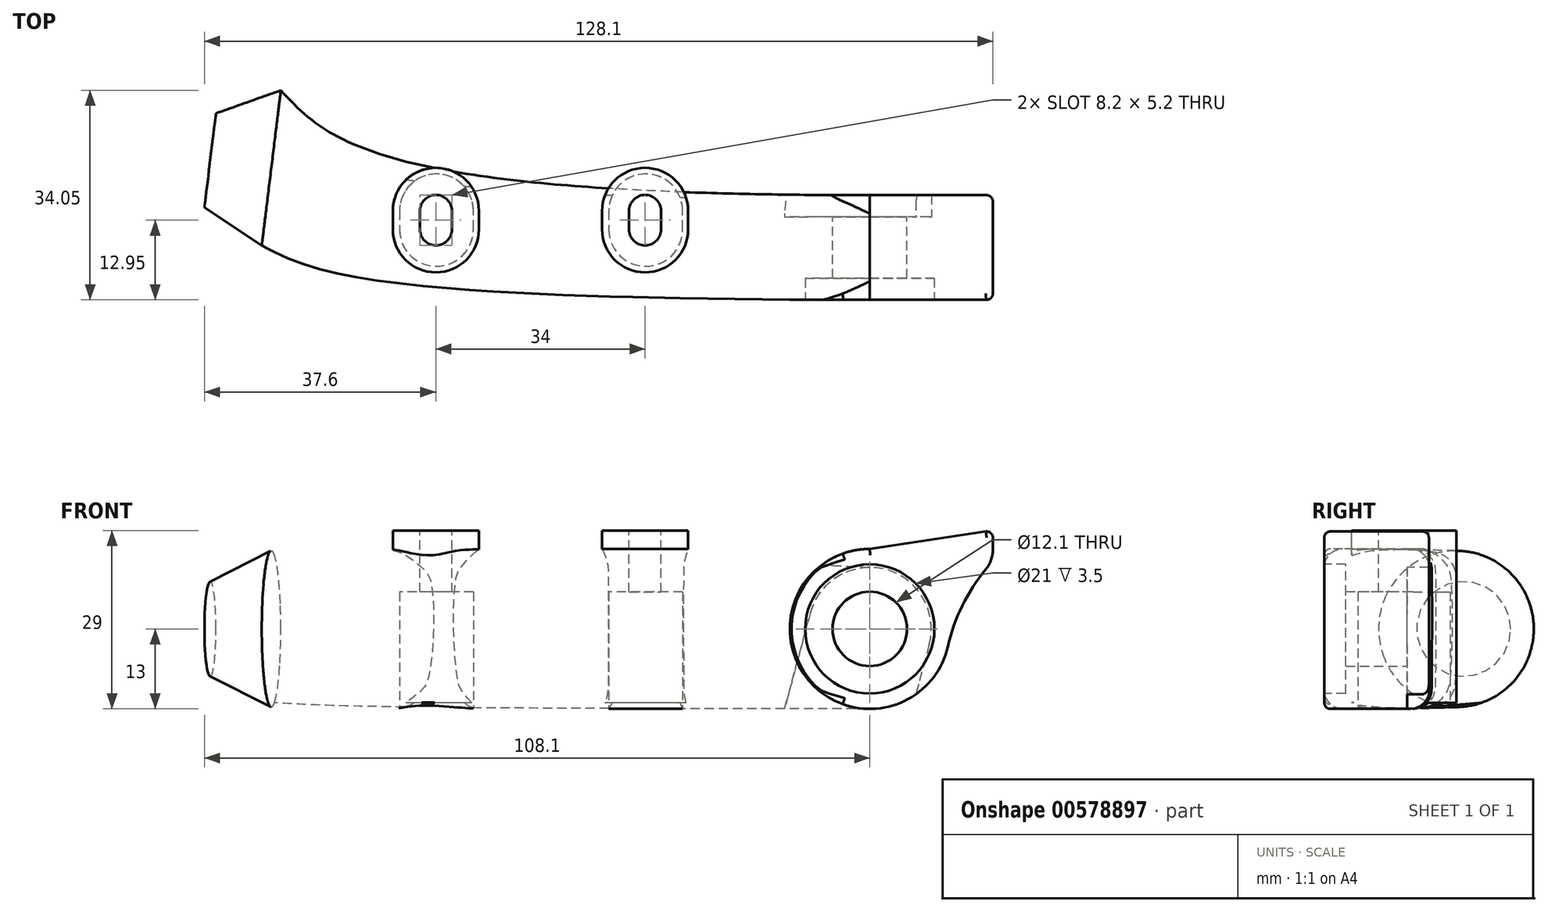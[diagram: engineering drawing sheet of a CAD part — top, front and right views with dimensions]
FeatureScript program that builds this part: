
annotation { "Feature Type Name" : "Feature", "Feature Type Description" : "" }
export const myFeature = defineFeature(function(context is Context, id is Id, definition is map)
    precondition{}
    {
        {
            var Q0;
            Q0=qCreatedBy(makeId("Top.planeOp"),FACE);
            cPlane(context, id + "F0", {"entities" : qUnion([Q0]), "cplaneType" : CPlaneType.OFFSET, "offset" : 16 * mm, "width" : 152.4 * mm, "height" : 152.4 * mm});
        }
        {
            var Q0;
            Q0=qCreatedBy(id+"F0.planeOp",FACE);
            var sketch = newSketch(context, id + "F1", { "sketchPlane" : qUnion([Q0])});
            skArc(sketch, "E0", {"start": v(-39.1, -2.05) * mm, "mid": v(-36.5, -4.65) * mm, "end": v(-33.9, -2.05) * mm});
            skArc(sketch, "E1", {"start": v(-33.9, 0.95) * mm, "mid": v(-36.5, 3.55) * mm, "end": v(-39.1, 0.95) * mm});
            skLineSegment(sketch, "E2", {"start": v(-39.1, -2.05) * mm, "end": v(-39.1, 0.95) * mm});
            skLineSegment(sketch, "E3", {"start": v(-33.9, 0.95) * mm, "end": v(-33.9, -2.05) * mm});
            skArc(sketch, "E4.0", {"start": v(-29.5, 0.95) * mm, "mid": v(-36.5, 7.95) * mm, "end": v(-43.5, 0.95) * mm});
            skLineSegment(sketch, "E4.1", {"start": v(-29.5, 0.95) * mm, "end": v(-29.5, -2.05) * mm});
            skArc(sketch, "E4.2", {"start": v(-43.5, -2.05) * mm, "mid": v(-36.5, -9.05) * mm, "end": v(-29.5, -2.05) * mm});
            skLineSegment(sketch, "E4.3", {"start": v(-43.5, -2.05) * mm, "end": v(-43.5, 0.95) * mm});
            skArc(sketch, "E5", {"start": v(-73.1, -2.05) * mm, "mid": v(-70.5, -4.65) * mm, "end": v(-67.9, -2.05) * mm});
            skArc(sketch, "E6", {"start": v(-67.9, 0.95) * mm, "mid": v(-70.5, 3.55) * mm, "end": v(-73.1, 0.95) * mm});
            skLineSegment(sketch, "E7", {"start": v(-73.1, -2.05) * mm, "end": v(-73.1, 0.95) * mm});
            skLineSegment(sketch, "E8", {"start": v(-67.9, 0.95) * mm, "end": v(-67.9, -2.05) * mm});
            skArc(sketch, "E9.0", {"start": v(-63.5, 0.95) * mm, "mid": v(-70.5, 7.95) * mm, "end": v(-77.5, 0.95) * mm});
            skLineSegment(sketch, "E9.1", {"start": v(-63.5, 0.95) * mm, "end": v(-63.5, -2.05) * mm});
            skArc(sketch, "E9.2", {"start": v(-77.5, -2.05) * mm, "mid": v(-70.5, -9.05) * mm, "end": v(-63.5, -2.05) * mm});
            skLineSegment(sketch, "E9.3", {"start": v(-77.5, -2.05) * mm, "end": v(-77.5, 0.95) * mm});
            skSolve(sketch);
        }
        {
            var Q0;
            Q0=makeQuery(id+"F1.imprint","IMPRINT",FACE,{"disambiguationData":[TD([[makeQuery(id+"F1.imprint","IMPRINT",EDGE,{"derivedFrom":sQuery(id+"F1.wireOp",EDGE,"E5")}),-1.0]])]});
            var Q1;
            Q1=makeQuery(id+"F1.imprint","IMPRINT",FACE,{"disambiguationData":[TD([[makeQuery(id+"F1.imprint","IMPRINT",EDGE,{"derivedFrom":sQuery(id+"F1.wireOp",EDGE,"E0")}),-1.0]])]});
            var Q2;
            {var subQ1=sQuery(id+"F9.wireOp",EDGE,"E18.bottom");var subQ2=sQuery(id+"F9.wireOp",EDGE,"E20.filletArc");var subQ3=sQuery(id+"F9.wireOp",EDGE,"E21.filletArc");var subQ4=sQuery(id+"F8.wireOp",EDGE,"E17");Q2=makeQuery(id+"F11.boolean.opBoolean","SPLIT",FACE,{"disambiguationData":[TD([makeQuery(id+"F11.opLoft","CAP_FACE",FACE,{"disambiguationData":[OSD([makeQuery(id+"F8.imprint","IMPRINT",FACE,{"disambiguationData":[TD([[makeQuery(id+"F8.imprint","IMPRINT",EDGE,{"derivedFrom":subQ4}),1.0]])]})])],"isStart":true})])],"derivedFrom":makeQuery(id+"F11.opLoft","SWEPT_FACE",FACE,{"disambiguationData":[OSD([subQ4,subQ1,subQ2,subQ3])]})});}
            var Q3;
            Q3=makeQuery(id+"F4.opExtrude","SWEPT_BODY",BODY,{"disambiguationData":[OSD([sQuery(id+"F3.wireOp",EDGE,"2tPzwoB9-yS2f-pc6b-ztwz-8XCjIK9uUhir"),sQuery(id+"F3.wireOp",EDGE,"E11"),sQuery(id+"F3.wireOp",EDGE,"te52xsig-TtHM-ymU2-F68U-3UsOK3ld5ssy"),sQuery(id+"F3.wireOp",EDGE,"6Uz9XqtG-uSJd-Klk5-Kt3H-MewUyz8nc5kr")])]});
            extrude(context, id + "F2", {"entities" : qUnion([Q0, Q1]), "oppositeDirection" : true, "depth" : 28 * mm, "endBoundEntityFace" : qUnion([Q2]), "endBoundEntityBody" : qUnion([Q3]), "offsetDistance" : 25 * mm});
        }
        {
            var Q0;
            Q0=qCreatedBy(makeId("Front.planeOp"),FACE);
            var sketch = newSketch(context, id + "F3", { "sketchPlane" : qUnion([Q0])});
            skCircle(sketch, "E10", {"center": v(0, 0) * mm, "radius": 6.05 * mm});
            skCircle(sketch, "E11", {"center": v(0, 0) * mm, "radius": 13 * mm});
            skArc(sketch, "E12", {"start": v(9.66, -2.59) * mm, "mid": v(2.59, 9.66) * mm, "end": v(-9.66, 2.59) * mm});
            skLineSegment(sketch, "E13", {"start": v(9.66, -2.59) * mm, "end": v(3.8, -24.44) * mm});
            skLineSegment(sketch, "E14", {"start": v(3.8, -24.44) * mm, "end": v(-15.51, -19.26) * mm});
            skLineSegment(sketch, "E15", {"start": v(-15.51, -19.26) * mm, "end": v(-9.66, 2.59) * mm});
            skSolve(sketch);
        }
        {
            var Q0;
            Q0=makeQuery(id+"F3.imprint","IMPRINT",FACE,{"disambiguationData":[TD([[makeQuery(id+"F3.imprint","IMPRINT",EDGE,{"derivedFrom":sQuery(id+"F3.wireOp",EDGE,"2tPzwoB9-yS2f-pc6b-ztwz-8XCjIK9uUhir")}),-1.0]])]});
            var Q1;
            {var subQ5=sQuery(id+"F3.wireOp",EDGE,"E12");Q1=makeQuery(id+"F3.imprint","IMPRINT",FACE,{"disambiguationData":[TD([[makeQuery(id+"F3.imprint","IMPRINT",EDGE,{"derivedFrom":subQ5}),-1.0]])]});}
            extrude(context, id + "F4", {"entities" : qUnion([Q0, Q1]), "oppositeDirection" : true, "depth" : 3.5 * mm, "offsetDistance" : 25 * mm});
        }
        {
            var Q0;
            Q0=makeQuery(id+"F3.imprint","IMPRINT",FACE,{"disambiguationData":[TD([[makeQuery(id+"F3.imprint","IMPRINT",EDGE,{"derivedFrom":sQuery(id+"F3.wireOp",EDGE,"E10")}),-1.0]])]});
            var Q1;
            {var subQ5=sQuery(id+"F3.wireOp",EDGE,"E12");Q1=makeQuery(id+"F3.imprint","IMPRINT",FACE,{"disambiguationData":[TD([[makeQuery(id+"F3.imprint","IMPRINT",EDGE,{"derivedFrom":subQ5}),-1.0]])]});}
            extrude(context, id + "F5", {"entities" : qUnion([Q0, Q1]), "operationType" : NewBodyOperationType.ADD, "depth" : 13.5 * mm, "offsetDistance" : 25 * mm});
        }
        {
            var Q0;
            Q0=qCreatedBy(makeId("Top.planeOp"),FACE);
            var sketch = newSketch(context, id + "F6", { "sketchPlane" : qUnion([Q0])});
            skLineSegment(sketch, "E16", {"start": v(-100, -14.56) * mm, "end": v(-96.9, 10.65) * mm});
            skSolve(sketch);
        }
        {
            var Q0;
            Q0=sQuery(id+"F6.wireOp",EDGE,"E16");
            cPlane(context, id + "F7", {"entities" : qUnion([Q0]), "cplaneType" : CPlaneType.LINE_ANGLE, "offset" : 25 * mm, "angle" : 90 * degree, "width" : 150 * mm, "height" : 150 * mm});
        }
        {
            var Q0;
            Q0=qCreatedBy(id+"F7.planeOp",FACE);
            var sketch = newSketch(context, id + "F8", { "sketchPlane" : qUnion([Q0])});
            skCircle(sketch, "E17", {"center": v(-3.97, 0) * mm, "radius": 12.7 * mm});
            skSolve(sketch);
        }
        {
            var Q0;
            Q0=qCreatedBy(makeId("Right.planeOp"),FACE);
            var sketch = newSketch(context, id + "F9", { "sketchPlane" : qUnion([Q0])});
            skLineSegment(sketch, "E18.bottom", {"start": v(0.5, -13) * mm, "end": v(-10.5, -13) * mm});
            skLineSegment(sketch, "E18.top", {"start": v(0.5, 13) * mm, "end": v(-10.5, 13) * mm});
            skLineSegment(sketch, "E18.left", {"start": v(3.5, -10) * mm, "end": v(3.5, 10) * mm});
            skLineSegment(sketch, "E18.right", {"start": v(-13.5, -10) * mm, "end": v(-13.5, 10) * mm});
            skPoint(sketch, "E19.visualSharp", {"position": v(-13.5, 13) * mm});
            skArc(sketch, "E19.filletArc", {"start": v(-10.5, 13) * mm, "mid": v(-12.62, 12.12) * mm, "end": v(-13.5, 10) * mm});
            skPoint(sketch, "E20.visualSharp", {"position": v(-13.5, -13) * mm});
            skArc(sketch, "E20.filletArc", {"start": v(-13.5, -10) * mm, "mid": v(-12.62, -12.12) * mm, "end": v(-10.5, -13) * mm});
            skPoint(sketch, "E21.visualSharp", {"position": v(3.5, -13) * mm});
            skArc(sketch, "E21.filletArc", {"start": v(0.5, -13) * mm, "mid": v(2.62, -12.12) * mm, "end": v(3.5, -10) * mm});
            skPoint(sketch, "E22.visualSharp", {"position": v(3.5, 13) * mm});
            skArc(sketch, "E22.filletArc", {"start": v(3.5, 10) * mm, "mid": v(2.62, 12.12) * mm, "end": v(0.5, 13) * mm});
            skSolve(sketch);
        }
        {
            var Q0;
            Q0=qCreatedBy(makeId("Right.planeOp"),FACE);
            cPlane(context, id + "F10", {"entities" : qUnion([Q0]), "cplaneType" : CPlaneType.OFFSET, "offset" : 20 * mm, "width" : 150 * mm, "height" : 150 * mm});
        }
        {
            var Q0;
            Q0 = qSketchRegion(id + "F9", true);
            var Q1;
            Q1 = qSketchRegion(id + "F8", true);
            loft(context, id + "F11", {"operationType" : NewBodyOperationType.ADD, "startCondition" : LoftEndDerivativeType.NORMAL_TO_PROFILE, "startMagnitude" : 2.5, "sheetProfilesArray" : [{ "sheetProfileEntities" : qUnion([Q0]) }, { "sheetProfileEntities" : qUnion([Q1]) }]});
        }
        {
            var Q0;
            Q0=qCreatedBy(makeId("Right.planeOp"),FACE);
            var sketch = newSketch(context, id + "F12", { "sketchPlane" : qUnion([Q0])});
            skLineSegment(sketch, "E23.bottom", {"start": v(3.5, 0) * mm, "end": v(-13.5, 0) * mm});
            skLineSegment(sketch, "E23.top", {"start": v(3.5, 13) * mm, "end": v(-13.5, 13) * mm});
            skLineSegment(sketch, "E23.left", {"start": v(3.5, 0) * mm, "end": v(3.5, 13) * mm});
            skLineSegment(sketch, "E23.right", {"start": v(-13.5, 0) * mm, "end": v(-13.5, 13) * mm});
            skPoint(sketch, "E24.visualSharp", {"position": v(-13.5, 13) * mm});
            skLineSegment(sketch, "E24.filletArc", {"start": v(-13.5, 13) * mm, "end": v(-13.5, 13) * mm});
            skPoint(sketch, "E25.visualSharp", {"position": v(3.5, 13) * mm});
            skLineSegment(sketch, "E25.filletArc", {"start": v(3.5, 13) * mm, "end": v(3.5, 13) * mm});
            skSolve(sketch);
        }
        {
            var Q0;
            Q0=qCreatedBy(id+"F10.planeOp",FACE);
            var sketch = newSketch(context, id + "F13", { "sketchPlane" : qUnion([Q0])});
            skLineSegment(sketch, "E26.bottom", {"start": v(3.5, 16) * mm, "end": v(-13.5, 16) * mm});
            skLineSegment(sketch, "E26.top", {"start": v(3.5, 11) * mm, "end": v(-13.5, 11) * mm});
            skLineSegment(sketch, "E26.left", {"start": v(3.5, 16) * mm, "end": v(3.5, 11) * mm});
            skLineSegment(sketch, "E26.right", {"start": v(-13.5, 16) * mm, "end": v(-13.5, 11) * mm});
            skSolve(sketch);
        }
        {
            var Q1;
            Q1 = qSketchRegion(id + "F12", true);
            var Q2;
            Q2 = qSketchRegion(id + "F13", true);
            loft(context, id + "F14", {"operationType" : NewBodyOperationType.ADD, "sheetProfilesArray" : [{ "sheetProfileEntities" : qUnion([Q1]) }, { "sheetProfileEntities" : qUnion([Q2]) }]});
        }
        {
            var Q0;
            Q0=makeQuery(id+"F3.imprint","IMPRINT",FACE,{"disambiguationData":[TD([[makeQuery(id+"F3.imprint","IMPRINT",EDGE,{"derivedFrom":sQuery(id+"F3.wireOp",EDGE,"E10")}),-1.0]])]});
            var Q1;
            {var subQ5=sQuery(id+"F3.wireOp",EDGE,"E14");Q1=makeQuery(id+"F3.imprint","IMPRINT",FACE,{"disambiguationData":[TD([[makeQuery(id+"F3.imprint","IMPRINT",EDGE,{"derivedFrom":subQ5}),-1.0]])]});}
            var Q2;
            Q2=makeQuery(id+"F3.imprint","IMPRINT",FACE,{"disambiguationData":[TD([[makeQuery(id+"F3.imprint","IMPRINT",EDGE,{"derivedFrom":sQuery(id+"F3.wireOp",EDGE,"E10")}),1.0]])]});
            extrude(context, id + "F15", {"entities" : qUnion([Q0, Q1, Q2]), "operationType" : NewBodyOperationType.REMOVE, "oppositeDirection" : true, "depth" : 25 * mm, "offsetDistance" : 25 * mm});
        }
        {
            var Q0;
            Q0=makeQuery(id+"F1.imprint","IMPRINT",FACE,{"disambiguationData":[TD([[makeQuery(id+"F1.imprint","IMPRINT",EDGE,{"derivedFrom":sQuery(id+"F1.wireOp",EDGE,"E5")}),1.0]])]});
            var Q1;
            Q1=makeQuery(id+"F1.imprint","IMPRINT",FACE,{"disambiguationData":[TD([[makeQuery(id+"F1.imprint","IMPRINT",EDGE,{"derivedFrom":sQuery(id+"F1.wireOp",EDGE,"E0")}),1.0]])]});
            extrude(context, id + "F16", {"entities" : qUnion([Q0, Q1]), "operationType" : NewBodyOperationType.REMOVE, "oppositeDirection" : true, "depth" : 30 * mm, "offsetDistance" : 25 * mm});
        }
        {
            var Q0;
            Q0=makeQuery(id+"F8.imprint","IMPRINT",FACE,{"disambiguationData":[TD([[makeQuery(id+"F8.imprint","IMPRINT",EDGE,{"derivedFrom":sQuery(id+"F8.wireOp",EDGE,"E17")}),1.0]])]});
            extrude(context, id + "F17", {"entities" : qUnion([Q0]), "operationType" : NewBodyOperationType.ADD, "oppositeDirection" : true, "depth" : 10 * mm, "offsetDistance" : 25 * mm});
        }
        {
            var Q0;
            Q0=makeQuery(id+"F17.opExtrude","CAP_EDGE",EDGE,{"disambiguationData":[OSD([sQuery(id+"F8.wireOp",EDGE,"E17")])],"isStart":false});
            chamfer(context, id + "F18", {"entities" : qUnion([Q0]), "chamferType" : ChamferType.TWO_OFFSETS, "width1" : 10 * mm, "oppositeDirection" : false, "width2" : 5 * mm, "tangentPropagation" : true});
        }
        {
            var Q0;
            Q0=makeQuery(id+"F3.imprint","IMPRINT",FACE,{"disambiguationData":[TD([[makeQuery(id+"F3.imprint","IMPRINT",EDGE,{"derivedFrom":sQuery(id+"F3.wireOp",EDGE,"E10")}),1.0]])]});
            extrude(context, id + "F19", {"entities" : qUnion([Q0]), "operationType" : NewBodyOperationType.REMOVE, "depth" : 25 * mm, "offsetDistance" : 25 * mm});
        }
        {
            var Q0;
            Q0=qCreatedBy(makeId("Top.planeOp"),FACE);
            cPlane(context, id + "F20", {"entities" : qUnion([Q0]), "cplaneType" : CPlaneType.OFFSET, "offset" : 30 * mm, "oppositeDirection" : true, "width" : 150 * mm, "height" : 150 * mm});
        }
        {
            var Q0;
            Q0=qCreatedBy(id+"F20.planeOp",FACE);
            var sketch = newSketch(context, id + "F21", { "sketchPlane" : qUnion([Q0])});
            skArc(sketch, "E27", {"start": v(-42.4, -2.05) * mm, "mid": v(-36.4, -8.05) * mm, "end": v(-30.4, -2.05) * mm});
            skArc(sketch, "E28", {"start": v(-30.4, 0.95) * mm, "mid": v(-36.4, 6.95) * mm, "end": v(-42.4, 0.95) * mm});
            skLineSegment(sketch, "E29", {"start": v(-42.4, 0.95) * mm, "end": v(-42.4, -2.05) * mm});
            skLineSegment(sketch, "E30", {"start": v(-30.4, -2.05) * mm, "end": v(-30.4, 0.95) * mm});
            skArc(sketch, "E31.1.0.0", {"start": v(-64.4, 0.95) * mm, "mid": v(-70.4, 6.95) * mm, "end": v(-76.4, 0.95) * mm});
            skLineSegment(sketch, "E31.1.0.1", {"start": v(-76.4, 0.95) * mm, "end": v(-76.4, -2.05) * mm});
            skArc(sketch, "E31.1.0.2", {"start": v(-76.4, -2.05) * mm, "mid": v(-70.4, -8.05) * mm, "end": v(-64.4, -2.05) * mm});
            skLineSegment(sketch, "E31.1.0.3", {"start": v(-64.4, -2.05) * mm, "end": v(-64.4, 0.95) * mm});
            skLineSegment(sketch, "E31.direction1", {"start": v(-76.4, -2.05) * mm, "end": v(-42.4, -2.05) * mm, "construction": true});
            skSolve(sketch);
        }
        {
            var Q0;
            Q0 = qSketchRegion(id + "F21", true);
            extrude(context, id + "F22", {"entities" : qUnion([Q0]), "operationType" : NewBodyOperationType.REMOVE, "depth" : 36 * mm, "offsetDistance" : 25 * mm});
        }
        {
            var Q0;
            Q0=makeQuery(id+"F5.opExtrude","CAP_FACE",FACE,{"disambiguationData":[OSD([sQuery(id+"F3.wireOp",EDGE,"E10"),sQuery(id+"F3.wireOp",EDGE,"E11")])],"isStart":false});
            var sketch = newSketch(context, id + "F23", { "sketchPlane" : qUnion([Q0])});
            skCircle(sketch, "E32", {"center": v(0, 0) * mm, "radius": 10.5 * mm});
            skSolve(sketch);
        }
        {
            var Q0;
            Q0 = qSketchRegion(id + "F23", true);
            extrude(context, id + "F24", {"entities" : qUnion([Q0]), "operationType" : NewBodyOperationType.REMOVE, "oppositeDirection" : true, "depth" : 3.5 * mm, "offsetDistance" : 25 * mm});
        }
        {
            var Q0;
            {var subQ0=sQuery(id+"F3.wireOp",EDGE,"E11");Q0=makeQuery(id+"F14.boolean.opBoolean","INTERSECT",EDGE,{"derivedFrom":[makeQuery(id+"F5.boolean.opBoolean","MERGE",FACE,{"derivedFrom":[makeQuery(id+"F4.opExtrude","SWEPT_FACE",FACE,{"disambiguationData":[OSD([subQ0])]}),makeQuery(id+"F5.opExtrude","SWEPT_FACE",FACE,{"disambiguationData":[OSD([subQ0])]})]}),makeQuery(id+"F14.opLoft","SWEPT_FACE",FACE,{"disambiguationData":[OSD([sQuery(id+"F12.wireOp",EDGE,"E23.bottom"),sQuery(id+"F12.wireOp",EDGE,"E23.left"),sQuery(id+"F12.wireOp",EDGE,"E23.right"),sQuery(id+"F13.wireOp",EDGE,"E26.top"),sQuery(id+"F13.wireOp",EDGE,"E26.left"),sQuery(id+"F13.wireOp",EDGE,"E26.right")])]})]});}
            fillet(context, id + "F25", {"entities" : qUnion([Q0]), "radius" : 30 * mm, "tangentPropagation" : true, "allowEdgeOverflow" : false});
        }
        {
            var Q0;
            {var subQ0=sQuery(id+"F13.wireOp",EDGE,"E26.top");var subQ1=sQuery(id+"F13.wireOp",EDGE,"E26.left");var subQ2=sQuery(id+"F13.wireOp",EDGE,"E26.right");var subQ3=sQuery(id+"F3.wireOp",EDGE,"E11");Q0=makeQuery(id+"F25.opFillet","BLEND_EDGE",EDGE,{"blendedFrom":[makeQuery(id+"F14.boolean.opBoolean","INTERSECT",EDGE,{"derivedFrom":[makeQuery(id+"F5.boolean.opBoolean","MERGE",FACE,{"derivedFrom":[makeQuery(id+"F4.opExtrude","SWEPT_FACE",FACE,{"disambiguationData":[OSD([subQ3])]}),makeQuery(id+"F5.opExtrude","SWEPT_FACE",FACE,{"disambiguationData":[OSD([subQ3])]})]}),makeQuery(id+"F14.opLoft","SWEPT_FACE",FACE,{"disambiguationData":[OSD([sQuery(id+"F12.wireOp",EDGE,"E23.bottom"),sQuery(id+"F12.wireOp",EDGE,"E23.left"),sQuery(id+"F12.wireOp",EDGE,"E23.right"),subQ0,subQ1,subQ2])]})]}),makeQuery(id+"F14.opLoft","CAP_FACE",FACE,{"disambiguationData":[OSD([makeQuery(id+"F13.imprint","IMPRINT",FACE,{"disambiguationData":[TD([[makeQuery(id+"F13.imprint","IMPRINT",EDGE,{"derivedFrom":sQuery(id+"F13.wireOp",EDGE,"E26.bottom")}),1.0]])]})])],"isStart":true})],"blendedInto":[makeQuery(id+"F14.opLoft","CAP_FACE",FACE,{"disambiguationData":[OSD([makeQuery(id+"F13.imprint","IMPRINT",FACE,{"disambiguationData":[TD([[makeQuery(id+"F13.imprint","IMPRINT",EDGE,{"derivedFrom":sQuery(id+"F13.wireOp",EDGE,"E26.bottom")}),1.0]])]})])],"isStart":true})]});}
            fillet(context, id + "F26", {"entities" : qUnion([Q0]), "radius" : 5 * mm, "tangentPropagation" : true, "allowEdgeOverflow" : false});
        }
        {
            var Q0;
            Q0=makeQuery(id+"F14.opLoft","SWEPT_EDGE",EDGE,{"disambiguationData":[OSD([sQuery(id+"F12.wireOp",EDGE,"E23.top"),sQuery(id+"F12.wireOp",EDGE,"E23.right"),sQuery(id+"F13.wireOp",EDGE,"E26.bottom"),sQuery(id+"F13.wireOp",EDGE,"E26.right")])]});
            var Q1;
            Q1=makeQuery(id+"F5.opExtrude","CAP_EDGE",EDGE,{"disambiguationData":[OSD([sQuery(id+"F3.wireOp",EDGE,"E11")])],"isStart":false});
            fillet(context, id + "F27", {"entities" : qUnion([Q0, Q1]), "radius" : 1 * mm, "tangentPropagation" : true, "allowEdgeOverflow" : false});
        }
        {
            var Q0;
            Q0=makeQuery(id+"F14.opLoft","MID_CAP_EDGE",EDGE,{"disambiguationData":[OSD([sQuery(id+"F13.wireOp",EDGE,"E26.bottom"),sQuery(id+"F13.wireOp",EDGE,"E26.left"),sQuery(id+"F13.wireOp",EDGE,"E26.right")])],"capPos":1.0});
            var Q1;
            Q1=makeQuery(id+"F14.opLoft","SWEPT_EDGE",EDGE,{"disambiguationData":[OSD([sQuery(id+"F12.wireOp",EDGE,"E23.top"),sQuery(id+"F12.wireOp",EDGE,"E23.left"),sQuery(id+"F13.wireOp",EDGE,"E26.bottom"),sQuery(id+"F13.wireOp",EDGE,"E26.left")])]});
            var Q2;
            {var subQ0=sQuery(id+"F13.wireOp",EDGE,"E26.left");var subQ1=sQuery(id+"F13.wireOp",EDGE,"E26.top");var subQ2=sQuery(id+"F12.wireOp",EDGE,"E23.left");var subQ3=sQuery(id+"F12.wireOp",EDGE,"E23.bottom");var subQ4=sQuery(id+"F3.wireOp",EDGE,"E11");Q2=makeQuery(id+"F25.opFillet","BLEND_EDGE",EDGE,{"blendedFrom":[makeQuery(id+"F14.boolean.opBoolean","INTERSECT",EDGE,{"derivedFrom":[makeQuery(id+"F5.boolean.opBoolean","MERGE",FACE,{"derivedFrom":[makeQuery(id+"F4.opExtrude","SWEPT_FACE",FACE,{"disambiguationData":[OSD([subQ4])]}),makeQuery(id+"F5.opExtrude","SWEPT_FACE",FACE,{"disambiguationData":[OSD([subQ4])]})]}),makeQuery(id+"F14.opLoft","SWEPT_FACE",FACE,{"disambiguationData":[OSD([subQ3,subQ2,sQuery(id+"F12.wireOp",EDGE,"E23.right"),subQ1,subQ0,sQuery(id+"F13.wireOp",EDGE,"E26.right")])]})]}),makeQuery(id+"F14.boolean.opBoolean","MERGE",FACE,{"derivedFrom":[makeQuery(id+"F4.opExtrude","CAP_FACE",FACE,{"disambiguationData":[OSD([subQ4,sQuery(id+"F3.wireOp",EDGE,"E12"),sQuery(id+"F3.wireOp",EDGE,"E13"),sQuery(id+"F3.wireOp",EDGE,"E15")])],"isStart":false}),makeQuery(id+"F14.opLoft","SWEPT_FACE",FACE,{"disambiguationData":[OSD([subQ3,sQuery(id+"F12.wireOp",EDGE,"E23.top"),subQ2,sQuery(id+"F13.wireOp",EDGE,"E26.bottom"),subQ1,subQ0])]})]})],"blendedInto":[makeQuery(id+"F14.boolean.opBoolean","MERGE",FACE,{"derivedFrom":[makeQuery(id+"F4.opExtrude","CAP_FACE",FACE,{"disambiguationData":[OSD([subQ4,sQuery(id+"F3.wireOp",EDGE,"E12"),sQuery(id+"F3.wireOp",EDGE,"E13"),sQuery(id+"F3.wireOp",EDGE,"E15")])],"isStart":false}),makeQuery(id+"F14.opLoft","SWEPT_FACE",FACE,{"disambiguationData":[OSD([subQ3,sQuery(id+"F12.wireOp",EDGE,"E23.top"),subQ2,sQuery(id+"F13.wireOp",EDGE,"E26.bottom"),subQ1,subQ0])]})]})]});}
            var Q3;
            {var subQ0=sQuery(id+"F3.wireOp",EDGE,"E11");var subQ1=sQuery(id+"F3.wireOp",EDGE,"E13");Q3=makeQuery(id+"F14.boolean.opBoolean","SPLIT",EDGE,{"disambiguationData":[TD([makeQuery(id+"F4.opExtrude","SWEPT_FACE",FACE,{"disambiguationData":[OSD([subQ1])]})])],"derivedFrom":makeQuery(id+"F4.opExtrude","CAP_EDGE",EDGE,{"disambiguationData":[OSD([subQ0])],"isStart":false})});}
            var Q4;
            {var subQ0=sQuery(id+"F13.wireOp",EDGE,"E26.left");var subQ1=sQuery(id+"F13.wireOp",EDGE,"E26.top");var subQ2=sQuery(id+"F13.wireOp",EDGE,"E26.bottom");var subQ3=sQuery(id+"F12.wireOp",EDGE,"E23.left");var subQ4=sQuery(id+"F12.wireOp",EDGE,"E23.bottom");var subQ5=sQuery(id+"F3.wireOp",EDGE,"E11");var subQ6=sQuery(id+"F13.wireOp",EDGE,"E26.right");Q4=makeQuery(id+"F26.opFillet","BLEND_EDGE",EDGE,{"blendedFrom":[makeQuery(id+"F25.opFillet","BLEND_EDGE",EDGE,{"blendedFrom":[makeQuery(id+"F14.boolean.opBoolean","INTERSECT",EDGE,{"derivedFrom":[makeQuery(id+"F5.boolean.opBoolean","MERGE",FACE,{"derivedFrom":[makeQuery(id+"F4.opExtrude","SWEPT_FACE",FACE,{"disambiguationData":[OSD([subQ5])]}),makeQuery(id+"F5.opExtrude","SWEPT_FACE",FACE,{"disambiguationData":[OSD([subQ5])]})]}),makeQuery(id+"F14.opLoft","SWEPT_FACE",FACE,{"disambiguationData":[OSD([subQ4,subQ3,sQuery(id+"F12.wireOp",EDGE,"E23.right"),subQ1,subQ0,subQ6])]})]}),makeQuery(id+"F14.opLoft","CAP_FACE",FACE,{"disambiguationData":[OSD([makeQuery(id+"F13.imprint","IMPRINT",FACE,{"disambiguationData":[TD([[makeQuery(id+"F13.imprint","IMPRINT",EDGE,{"derivedFrom":subQ2}),1.0]])]})])],"isStart":true})],"blendedInto":[makeQuery(id+"F14.opLoft","CAP_FACE",FACE,{"disambiguationData":[OSD([makeQuery(id+"F13.imprint","IMPRINT",FACE,{"disambiguationData":[TD([[makeQuery(id+"F13.imprint","IMPRINT",EDGE,{"derivedFrom":subQ2}),1.0]])]})])],"isStart":true})]}),makeQuery(id+"F14.boolean.opBoolean","MERGE",FACE,{"derivedFrom":[makeQuery(id+"F4.opExtrude","CAP_FACE",FACE,{"disambiguationData":[OSD([subQ5,sQuery(id+"F3.wireOp",EDGE,"E12"),sQuery(id+"F3.wireOp",EDGE,"E13"),sQuery(id+"F3.wireOp",EDGE,"E15")])],"isStart":false}),makeQuery(id+"F14.opLoft","SWEPT_FACE",FACE,{"disambiguationData":[OSD([subQ4,sQuery(id+"F12.wireOp",EDGE,"E23.top"),subQ3,subQ2,subQ1,subQ0])]})]})],"blendedInto":[makeQuery(id+"F14.boolean.opBoolean","MERGE",FACE,{"derivedFrom":[makeQuery(id+"F4.opExtrude","CAP_FACE",FACE,{"disambiguationData":[OSD([subQ5,sQuery(id+"F3.wireOp",EDGE,"E12"),sQuery(id+"F3.wireOp",EDGE,"E13"),sQuery(id+"F3.wireOp",EDGE,"E15")])],"isStart":false}),makeQuery(id+"F14.opLoft","SWEPT_FACE",FACE,{"disambiguationData":[OSD([subQ4,sQuery(id+"F12.wireOp",EDGE,"E23.top"),subQ3,subQ2,subQ1,subQ0])]})]})]});}
            var Q5;
            {var subQ0=sQuery(id+"F3.wireOp",EDGE,"E11");Q5=makeQuery(id+"F14.boolean.opBoolean","SPLIT",EDGE,{"disambiguationData":[TD([makeQuery(id+"F11.opLoft","SWEPT_FACE",FACE,{"disambiguationData":[OSD([sQuery(id+"F8.wireOp",EDGE,"E17"),sQuery(id+"F9.wireOp",EDGE,"E18.bottom"),sQuery(id+"F9.wireOp",EDGE,"E20.filletArc"),sQuery(id+"F9.wireOp",EDGE,"E21.filletArc")])]})])],"derivedFrom":makeQuery(id+"F4.opExtrude","CAP_EDGE",EDGE,{"disambiguationData":[OSD([subQ0])],"isStart":false})});}
            fillet(context, id + "F28", {"entities" : qUnion([Q0, Q1, Q2, Q3, Q4, Q5]), "radius" : 1 * mm, "tangentPropagation" : true, "allowEdgeOverflow" : false});
        }
    });
